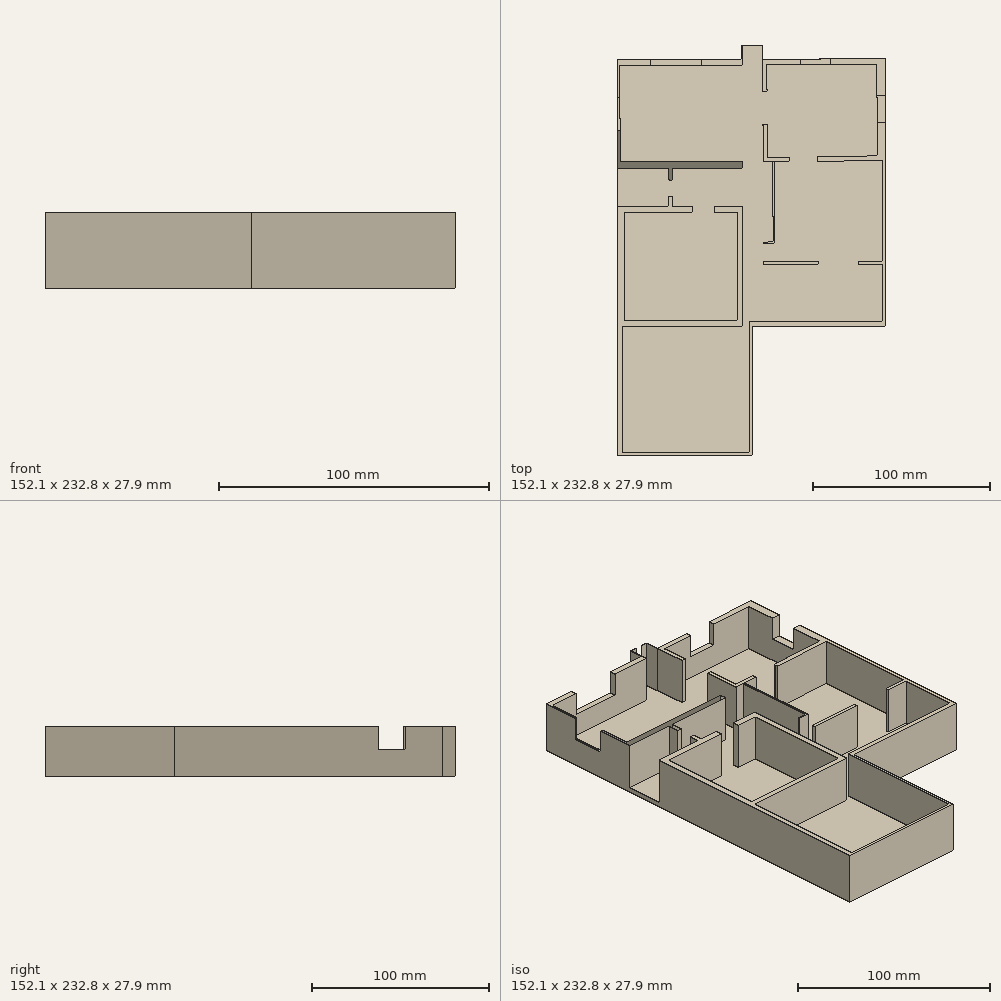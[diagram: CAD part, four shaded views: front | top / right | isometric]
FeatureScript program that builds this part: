
annotation { "Feature Type Name" : "Feature", "Feature Type Description" : "" }
export const myFeature = defineFeature(function(context is Context, id is Id, definition is map)
    precondition{}
    {
        {
            var Q0;
            Q0=qCreatedBy(makeId("Top.planeOp"),FACE);
            var sketch = newSketch(context, id + "F0", { "sketchPlane" : qUnion([Q0])});
            skLineSegment(sketch, "E0", {"start": v(0, 0) * mm, "end": v(0, 75.35) * mm});
            skLineSegment(sketch, "E1", {"start": v(0, 75.35) * mm, "end": v(-76.45, 75.35) * mm});
            skLineSegment(sketch, "E2", {"start": v(-76.45, 75.35) * mm, "end": v(-76.45, 0) * mm});
            skLineSegment(sketch, "E3", {"start": v(-76.45, 0) * mm, "end": v(-76.45, -76.07) * mm});
            skLineSegment(sketch, "E4", {"start": v(-76.45, -76.07) * mm, "end": v(0, -76.07) * mm});
            skLineSegment(sketch, "E5", {"start": v(0, -76.07) * mm, "end": v(0, 0) * mm});
            skLineSegment(sketch, "E6", {"start": v(0, -76.07) * mm, "end": v(75.68, -76.07) * mm});
            skLineSegment(sketch, "E7", {"start": v(75.68, -76.07) * mm, "end": v(75.68, 76.2) * mm});
            skLineSegment(sketch, "E8", {"start": v(75.68, 76.2) * mm, "end": v(0, 75.35) * mm});
            skLineSegment(sketch, "E9", {"start": v(0, 0) * mm, "end": v(75.68, 0) * mm});
            skLineSegment(sketch, "E10", {"start": v(0, 0) * mm, "end": v(-76.45, 0) * mm});
            skSolve(sketch);
        }
        {
            var Q0;
            Q0 = qSketchRegion(id + "F0", true);
            extrude(context, id + "F1", {"entities" : qUnion([Q0]), "depth" : 2.54 * mm, "offsetDistance" : 25.4 * mm});
        }
        {
            var Q0;
            Q0=makeQuery(id+"F1.opExtrude","CAP_FACE",FACE,{"disambiguationData":[OSD([sQuery(id+"F0.wireOp",EDGE,"E1"),sQuery(id+"F0.wireOp",EDGE,"E2"),sQuery(id+"F0.wireOp",EDGE,"E3"),sQuery(id+"F0.wireOp",EDGE,"E4"),sQuery(id+"F0.wireOp",EDGE,"E6"),sQuery(id+"F0.wireOp",EDGE,"E7"),sQuery(id+"F0.wireOp",EDGE,"E8")])],"isStart":false});
            var sketch = newSketch(context, id + "F2", { "sketchPlane" : qUnion([Q0])});
            skLineSegment(sketch, "E11.0", {"start": v(0, 0) * mm, "end": v(0, 75.35) * mm});
            skLineSegment(sketch, "E12.0", {"start": v(0, -76.07) * mm, "end": v(0, 0) * mm});
            skLineSegment(sketch, "E13", {"start": v(0, 75.35) * mm, "end": v(-5.93, 75.35) * mm});
            skLineSegment(sketch, "E14", {"start": v(-5.93, 75.35) * mm, "end": v(-5.93, 83.46) * mm});
            skLineSegment(sketch, "E15", {"start": v(-5.93, 83.46) * mm, "end": v(0, 83.46) * mm});
            skLineSegment(sketch, "E16", {"start": v(0, 83.46) * mm, "end": v(5.93, 83.46) * mm});
            skLineSegment(sketch, "E17", {"start": v(5.93, 83.46) * mm, "end": v(5.93, 75.35) * mm});
            skLineSegment(sketch, "E18", {"start": v(5.93, 75.35) * mm, "end": v(0, 75.35) * mm});
            skSolve(sketch);
        }
        {
            var Q0;
            Q0 = qSketchRegion(id + "F2", true);
            extrude(context, id + "F3", {"entities" : qUnion([Q0]), "operationType" : NewBodyOperationType.ADD, "oppositeDirection" : true, "depth" : 2.54 * mm, "offsetDistance" : 25.4 * mm});
        }
        {
            var Q0;
            Q0=makeQuery(id+"F3.boolean.opBoolean","MERGE",FACE,{"derivedFrom":[makeQuery(id+"F1.opExtrude","CAP_FACE",FACE,{"disambiguationData":[OSD([sQuery(id+"F0.wireOp",EDGE,"E1"),sQuery(id+"F0.wireOp",EDGE,"E2"),sQuery(id+"F0.wireOp",EDGE,"E3"),sQuery(id+"F0.wireOp",EDGE,"E4"),sQuery(id+"F0.wireOp",EDGE,"E6"),sQuery(id+"F0.wireOp",EDGE,"E7"),sQuery(id+"F0.wireOp",EDGE,"E8")])],"isStart":false}),makeQuery(id+"F3.opExtrude","CAP_FACE",FACE,{"disambiguationData":[OSD([sQuery(id+"F2.wireOp",EDGE,"E13"),sQuery(id+"F2.wireOp",EDGE,"E14"),sQuery(id+"F2.wireOp",EDGE,"E15"),sQuery(id+"F2.wireOp",EDGE,"E16"),sQuery(id+"F2.wireOp",EDGE,"E17"),sQuery(id+"F2.wireOp",EDGE,"E18")])],"isStart":true})]});
            var sketch = newSketch(context, id + "F4", { "sketchPlane" : qUnion([Q0])});
            skLineSegment(sketch, "E19.0", {"start": v(0, 0) * mm, "end": v(0, 75.35) * mm});
            skLineSegment(sketch, "E20.0", {"start": v(0, -76.07) * mm, "end": v(0, 0) * mm});
            skPoint(sketch, "E21.0", {"position": v(5.93, 75.42) * mm});
            skLineSegment(sketch, "E22", {"start": v(5.93, 75.42) * mm, "end": v(6.14, 57.18) * mm});
            skLineSegment(sketch, "E23", {"start": v(5.93, 75.42) * mm, "end": v(8.22, 75.45) * mm});
            skLineSegment(sketch, "E24", {"start": v(8.22, 75.45) * mm, "end": v(8.43, 57.18) * mm});
            skLineSegment(sketch, "E25", {"start": v(8.43, 57.18) * mm, "end": v(6.14, 57.18) * mm});
            skLineSegment(sketch, "E26", {"start": v(6.14, 38.62) * mm, "end": v(6.31, 22.93) * mm});
            skLineSegment(sketch, "E27", {"start": v(6.31, 22.93) * mm, "end": v(8.43, 22.96) * mm});
            skLineSegment(sketch, "E28", {"start": v(8.43, 22.96) * mm, "end": v(8.43, 38.62) * mm});
            skLineSegment(sketch, "E29", {"start": v(8.43, 38.62) * mm, "end": v(6.14, 38.62) * mm});
            skLineSegment(sketch, "E30", {"start": v(6.31, 22.93) * mm, "end": v(6.38, 17.54) * mm});
            skLineSegment(sketch, "E31", {"start": v(6.38, 17.54) * mm, "end": v(21.15, 17.71) * mm});
            skLineSegment(sketch, "E32", {"start": v(21.15, 17.71) * mm, "end": v(21.12, 19.99) * mm});
            skLineSegment(sketch, "E33", {"start": v(21.12, 19.99) * mm, "end": v(8.43, 19.84) * mm});
            skLineSegment(sketch, "E34", {"start": v(8.43, 19.84) * mm, "end": v(8.43, 22.96) * mm});
            skLineSegment(sketch, "E35", {"start": v(37.2, 17.71) * mm, "end": v(75.68, 18.15) * mm});
            skLineSegment(sketch, "E36", {"start": v(75.68, 18.15) * mm, "end": v(75.68, 19.99) * mm});
            skLineSegment(sketch, "E37", {"start": v(75.68, 19.99) * mm, "end": v(37.1, 19.55) * mm});
            skLineSegment(sketch, "E38", {"start": v(37.1, 19.55) * mm, "end": v(37.2, 17.71) * mm});
            skLineSegment(sketch, "E39", {"start": v(8.25, 72.63) * mm, "end": v(70.66, 72.63) * mm});
            skLineSegment(sketch, "E40", {"start": v(70.66, 72.63) * mm, "end": v(70.66, 76.15) * mm});
            skLineSegment(sketch, "E41", {"start": v(70.66, 76.15) * mm, "end": v(8.22, 75.45) * mm});
            skLineSegment(sketch, "E42", {"start": v(70.66, 72.63) * mm, "end": v(71.25, 19.99) * mm});
            skLineSegment(sketch, "E43", {"start": v(71.25, 19.99) * mm, "end": v(75.68, 19.99) * mm});
            skLineSegment(sketch, "E44", {"start": v(75.68, 19.99) * mm, "end": v(75.68, 76.2) * mm});
            skLineSegment(sketch, "E45", {"start": v(71.03, 39.78) * mm, "end": v(75.68, 39.83) * mm});
            skLineSegment(sketch, "E46", {"start": v(70.86, 55.15) * mm, "end": v(75.68, 55.15) * mm});
            skLineSegment(sketch, "E47", {"start": v(27.72, 72.63) * mm, "end": v(27.69, 75.67) * mm});
            skLineSegment(sketch, "E48", {"start": v(44.66, 72.63) * mm, "end": v(44.63, 75.86) * mm});
            skLineSegment(sketch, "E49", {"start": v(6.38, -38.96) * mm, "end": v(37.4, -38.96) * mm});
            skLineSegment(sketch, "E50", {"start": v(60.62, -38.96) * mm, "end": v(75.68, -38.96) * mm});
            skLineSegment(sketch, "E51", {"start": v(75.68, -38.96) * mm, "end": v(75.68, 18.15) * mm});
            skLineSegment(sketch, "E52", {"start": v(6.38, -38.96) * mm, "end": v(6.38, -46.95) * mm});
            skLineSegment(sketch, "E53", {"start": v(6.38, -76.07) * mm, "end": v(75.68, -76.07) * mm});
            skLineSegment(sketch, "E54", {"start": v(75.68, -76.07) * mm, "end": v(75.68, -38.96) * mm});
            skLineSegment(sketch, "E55", {"start": v(8.43, -28.89) * mm, "end": v(6.38, -28.89) * mm});
            skLineSegment(sketch, "E56", {"start": v(73.78, 18.13) * mm, "end": v(73.78, -38.96) * mm});
            skLineSegment(sketch, "E57", {"start": v(6.38, -40.7) * mm, "end": v(37.4, -40.7) * mm});
            skLineSegment(sketch, "E58", {"start": v(37.4, -40.7) * mm, "end": v(37.4, -38.96) * mm});
            skLineSegment(sketch, "E59", {"start": v(60.62, -40.7) * mm, "end": v(75.68, -40.7) * mm});
            skLineSegment(sketch, "E60", {"start": v(60.62, -40.7) * mm, "end": v(60.62, -38.96) * mm});
            skLineSegment(sketch, "E61", {"start": v(73.78, -40.7) * mm, "end": v(73.78, -73.26) * mm});
            skLineSegment(sketch, "E62", {"start": v(73.78, -73.26) * mm, "end": v(6.38, -73.26) * mm});
            skLineSegment(sketch, "E63", {"start": v(6.38, -73.26) * mm, "end": v(6.38, -76.07) * mm});
            skLineSegment(sketch, "E64", {"start": v(-5.93, 83.46) * mm, "end": v(-2.26, 83.46) * mm});
            skLineSegment(sketch, "E65", {"start": v(-5.46, 82.76) * mm, "end": v(-5.93, 82.76) * mm});
            skLineSegment(sketch, "E66", {"start": v(-5.93, 82.76) * mm, "end": v(-5.93, 83.46) * mm});
            skLineSegment(sketch, "E67", {"start": v(-5.93, 82.76) * mm, "end": v(-5.93, 75.35) * mm});
            skLineSegment(sketch, "E68", {"start": v(-5.93, 75.35) * mm, "end": v(-5.46, 75.35) * mm});
            skLineSegment(sketch, "E69", {"start": v(-5.46, 75.35) * mm, "end": v(-5.46, 82.76) * mm});
            skLineSegment(sketch, "E70", {"start": v(5.93, 75.42) * mm, "end": v(5.93, 83.46) * mm});
            skLineSegment(sketch, "E71", {"start": v(5.93, 83.46) * mm, "end": v(1.63, 83.46) * mm});
            skLineSegment(sketch, "E72", {"start": v(-5.93, 75.35) * mm, "end": v(-76.45, 75.35) * mm});
            skLineSegment(sketch, "E73", {"start": v(-76.45, 75.35) * mm, "end": v(-76.45, 71.98) * mm});
            skLineSegment(sketch, "E74", {"start": v(-76.45, 71.98) * mm, "end": v(-5.46, 71.98) * mm});
            skLineSegment(sketch, "E75", {"start": v(-5.46, 71.98) * mm, "end": v(-5.46, 75.35) * mm});
            skLineSegment(sketch, "E76", {"start": v(-5.46, 17.54) * mm, "end": v(-76.45, 17.54) * mm});
            skLineSegment(sketch, "E77", {"start": v(-5.46, 17.54) * mm, "end": v(-5.41, 13.55) * mm});
            skLineSegment(sketch, "E78", {"start": v(-5.41, 13.55) * mm, "end": v(-76.45, 13.55) * mm});
            skLineSegment(sketch, "E79", {"start": v(-76.45, 13.55) * mm, "end": v(-76.45, 17.54) * mm});
            skLineSegment(sketch, "E80", {"start": v(-5.41, -7.79) * mm, "end": v(-21.24, -7.97) * mm});
            skLineSegment(sketch, "E81", {"start": v(-5.41, -7.79) * mm, "end": v(-5.41, -76.07) * mm});
            skLineSegment(sketch, "E82", {"start": v(-33.79, -7.97) * mm, "end": v(-76.45, -7.97) * mm});
            skLineSegment(sketch, "E83", {"start": v(-76.45, -7.97) * mm, "end": v(-76.45, -11.38) * mm});
            skLineSegment(sketch, "E84", {"start": v(-76.45, -11.38) * mm, "end": v(-33.79, -11.38) * mm});
            skLineSegment(sketch, "E85", {"start": v(-33.79, -11.38) * mm, "end": v(-33.79, -7.97) * mm});
            skLineSegment(sketch, "E86", {"start": v(-21.24, -11.38) * mm, "end": v(-8.58, -11.38) * mm});
            skLineSegment(sketch, "E87", {"start": v(-8.58, -11.38) * mm, "end": v(-8.58, -76.07) * mm});
            skLineSegment(sketch, "E88", {"start": v(-8.58, -76.07) * mm, "end": v(-5.41, -76.07) * mm});
            skLineSegment(sketch, "E89", {"start": v(-21.24, -11.38) * mm, "end": v(-21.24, -7.97) * mm});
            skLineSegment(sketch, "E90", {"start": v(-72.71, -11.38) * mm, "end": v(-72.71, -72.9) * mm});
            skLineSegment(sketch, "E91", {"start": v(-72.71, -72.9) * mm, "end": v(-8.58, -72.9) * mm});
            skLineSegment(sketch, "E92.0", {"start": v(75.68, 76.2) * mm, "end": v(0, 75.35) * mm});
            skLineSegment(sketch, "E93.0", {"start": v(-76.45, 0) * mm, "end": v(-76.45, -76.07) * mm});
            skLineSegment(sketch, "E94", {"start": v(-44.97, 13.55) * mm, "end": v(-44.97, 7) * mm});
            skLineSegment(sketch, "E95", {"start": v(-44.97, -7.97) * mm, "end": v(-44.97, -2.33) * mm});
            skLineSegment(sketch, "E96", {"start": v(-47.46, 13.55) * mm, "end": v(-47.46, 7.13) * mm});
            skLineSegment(sketch, "E97", {"start": v(-44.97, 7) * mm, "end": v(-47.46, 7.13) * mm});
            skLineSegment(sketch, "E98", {"start": v(-44.97, -2.33) * mm, "end": v(-47.46, -2.33) * mm});
            skLineSegment(sketch, "E99", {"start": v(-47.46, -2.33) * mm, "end": v(-47.46, -7.97) * mm});
            skLineSegment(sketch, "E100", {"start": v(75.68, 19.99) * mm, "end": v(75.68, 39.83) * mm});
            skLineSegment(sketch, "E101", {"start": v(75.68, 39.83) * mm, "end": v(75.68, 55.15) * mm});
            skLineSegment(sketch, "E102", {"start": v(75.68, 55.15) * mm, "end": v(75.68, 76.2) * mm});
            skLineSegment(sketch, "E103", {"start": v(8.22, 75.45) * mm, "end": v(27.69, 75.67) * mm});
            skLineSegment(sketch, "E104", {"start": v(27.69, 75.67) * mm, "end": v(44.63, 75.86) * mm});
            skLineSegment(sketch, "E105", {"start": v(44.63, 75.86) * mm, "end": v(70.66, 76.15) * mm});
            skLineSegment(sketch, "E106", {"start": v(70.66, 76.15) * mm, "end": v(75.68, 76.2) * mm});
            skLineSegment(sketch, "E107", {"start": v(75.79, 76.24) * mm, "end": v(75.68, 55.15) * mm});
            skLineSegment(sketch, "E108", {"start": v(-75.4, 71.98) * mm, "end": v(-74.78, 17.54) * mm});
            skLineSegment(sketch, "E109", {"start": v(-76.45, 17.54) * mm, "end": v(-76.45, 71.98) * mm});
            skLineSegment(sketch, "E110", {"start": v(-75.2, 54.08) * mm, "end": v(-76.45, 54.08) * mm});
            skLineSegment(sketch, "E111", {"start": v(-76.45, 54.08) * mm, "end": v(-76.45, 35.02) * mm});
            skLineSegment(sketch, "E112", {"start": v(-76.45, 35.02) * mm, "end": v(-74.98, 35.04) * mm});
            skLineSegment(sketch, "E113", {"start": v(-74.98, 35.04) * mm, "end": v(-75.2, 54.08) * mm});
            skLineSegment(sketch, "E114", {"start": v(-72.71, -23.63) * mm, "end": v(-76.45, -23.63) * mm});
            skLineSegment(sketch, "E115", {"start": v(-76.45, -23.63) * mm, "end": v(-76.45, -32.25) * mm});
            skLineSegment(sketch, "E116", {"start": v(-76.45, -32.25) * mm, "end": v(-72.71, -32.2) * mm});
            skLineSegment(sketch, "E117", {"start": v(-72.71, -32.2) * mm, "end": v(-72.71, -23.63) * mm});
            skLineSegment(sketch, "E118", {"start": v(20.11, -73.26) * mm, "end": v(20.14, -76.07) * mm});
            skLineSegment(sketch, "E119", {"start": v(20.14, -76.07) * mm, "end": v(56.16, -76.07) * mm});
            skLineSegment(sketch, "E120", {"start": v(56.16, -76.07) * mm, "end": v(56.13, -73.26) * mm});
            skLineSegment(sketch, "E121", {"start": v(56.13, -73.26) * mm, "end": v(20.11, -73.26) * mm});
            skLineSegment(sketch, "E122", {"start": v(-28.91, 75.35) * mm, "end": v(-28.91, 71.98) * mm});
            skLineSegment(sketch, "E123", {"start": v(-28.91, 71.98) * mm, "end": v(-57.74, 71.98) * mm});
            skLineSegment(sketch, "E124", {"start": v(-57.74, 71.98) * mm, "end": v(-57.74, 75.35) * mm});
            skLineSegment(sketch, "E125", {"start": v(-76.45, 0) * mm, "end": v(-76.45, 13.55) * mm});
            skLineSegment(sketch, "E126", {"start": v(-76.45, 13.55) * mm, "end": v(-76.45, -7.97) * mm});
            skLineSegment(sketch, "E127", {"start": v(-76.45, -7.97) * mm, "end": v(-75.89, -7.97) * mm});
            skLineSegment(sketch, "E128", {"start": v(-75.89, -7.97) * mm, "end": v(-75.89, 13.55) * mm});
            skLineSegment(sketch, "E129", {"start": v(-75.89, 13.55) * mm, "end": v(-76.45, 13.55) * mm});
            skLineSegment(sketch, "E130", {"start": v(6.38, -73.26) * mm, "end": v(0, -73.26) * mm});
            skLineSegment(sketch, "E131", {"start": v(0, -73.26) * mm, "end": v(0, -76.07) * mm});
            skLineSegment(sketch, "E132", {"start": v(0, -76.07) * mm, "end": v(6.38, -76.07) * mm});
            skPoint(sketch, "E133.end.orphan", {"position": v(1.63, 82.76) * mm});
            skLineSegment(sketch, "E134", {"start": v(-5.46, 82.76) * mm, "end": v(-5.46, 83.2) * mm});
            skLineSegment(sketch, "E135", {"start": v(-5.46, 83.2) * mm, "end": v(-2.26, 83.2) * mm});
            skLineSegment(sketch, "E136", {"start": v(-2.26, 83.2) * mm, "end": v(-2.26, 83.46) * mm});
            skLineSegment(sketch, "E137", {"start": v(1.63, 83.2) * mm, "end": v(5.69, 83.2) * mm});
            skLineSegment(sketch, "E138", {"start": v(5.69, 83.2) * mm, "end": v(5.69, 75.42) * mm});
            skLineSegment(sketch, "E139", {"start": v(1.63, 83.46) * mm, "end": v(1.63, 83.2) * mm});
            skPoint(sketch, "E140.end.orphan", {"position": v(5.34, 75.35) * mm});
            skLineSegment(sketch, "E141", {"start": v(5.69, 75.42) * mm, "end": v(5.93, 75.42) * mm});
            skPoint(sketch, "E142.start.orphan", {"position": v(8.43, 17.57) * mm});
            skLineSegment(sketch, "E143", {"start": v(8.43, -28.89) * mm, "end": v(12.92, -28.89) * mm});
            skLineSegment(sketch, "E144", {"start": v(12.92, -28.89) * mm, "end": v(12.4, 17.61) * mm});
            skLineSegment(sketch, "E145", {"start": v(12.4, 17.61) * mm, "end": v(11.47, 17.6) * mm});
            skLineSegment(sketch, "E146", {"start": v(11.47, 17.6) * mm, "end": v(12, -28.89) * mm});
            skLineSegment(sketch, "E147", {"start": v(12, -28.89) * mm, "end": v(12.92, -28.89) * mm});
            skSolve(sketch);
        }
        {
            var Q0;
            Q0=makeQuery(id+"F0.imprint","IMPRINT",FACE,{"disambiguationData":[TD([[makeQuery(id+"F0.imprint","IMPRINT",EDGE,{"derivedFrom":sQuery(id+"F0.wireOp",EDGE,"E0")}),-1.0]])]});
            var sketch = newSketch(context, id + "F5", { "sketchPlane" : qUnion([Q0])});
            skLineSegment(sketch, "E148.0", {"start": v(0, -76.07) * mm, "end": v(75.68, -76.07) * mm});
            skLineSegment(sketch, "E149.0.3", {"start": v(-72.71, -11.38) * mm, "end": v(-76.45, -11.38) * mm});
            skLineSegment(sketch, "E149.0.4", {"start": v(-76.45, -11.38) * mm, "end": v(-76.45, -23.63) * mm});
            skLineSegment(sketch, "E150", {"start": v(0, -76.07) * mm, "end": v(0, -149.33) * mm});
            skLineSegment(sketch, "E151", {"start": v(0, -149.33) * mm, "end": v(-76.45, -149.33) * mm});
            skLineSegment(sketch, "E152", {"start": v(-76.45, -149.33) * mm, "end": v(-76.45, -23.63) * mm});
            skLineSegment(sketch, "E153", {"start": v(0, -76.07) * mm, "end": v(-76.45, -76.07) * mm});
            skPoint(sketch, "E149.0.0.start.orphan", {"position": v(-8.58, -23.63) * mm});
            skSolve(sketch);
        }
        {
            var Q0;
            {var subQ3=sQuery(id+"F5.wireOp",EDGE,"E150");Q0=makeQuery(id+"F5.imprint","IMPRINT",FACE,{"disambiguationData":[TD([[makeQuery(id+"F5.imprint","IMPRINT",EDGE,{"derivedFrom":subQ3}),-1.0]])]});}
            extrude(context, id + "F6", {"entities" : qUnion([Q0]), "operationType" : NewBodyOperationType.ADD, "depth" : 2.54 * mm, "offsetDistance" : 25.4 * mm});
        }
        {
            var Q0;
            Q0=makeQuery(id+"F6.boolean.opBoolean","MERGE",FACE,{"derivedFrom":[makeQuery(id+"F3.boolean.opBoolean","MERGE",FACE,{"derivedFrom":[makeQuery(id+"F1.opExtrude","CAP_FACE",FACE,{"disambiguationData":[OSD([sQuery(id+"F0.wireOp",EDGE,"E1"),sQuery(id+"F0.wireOp",EDGE,"E2"),sQuery(id+"F0.wireOp",EDGE,"E3"),sQuery(id+"F0.wireOp",EDGE,"E4"),sQuery(id+"F0.wireOp",EDGE,"E6"),sQuery(id+"F0.wireOp",EDGE,"E7"),sQuery(id+"F0.wireOp",EDGE,"E8")])],"isStart":false}),makeQuery(id+"F3.opExtrude","CAP_FACE",FACE,{"disambiguationData":[OSD([sQuery(id+"F2.wireOp",EDGE,"E13"),sQuery(id+"F2.wireOp",EDGE,"E14"),sQuery(id+"F2.wireOp",EDGE,"E15"),sQuery(id+"F2.wireOp",EDGE,"E16"),sQuery(id+"F2.wireOp",EDGE,"E17"),sQuery(id+"F2.wireOp",EDGE,"E18")])],"isStart":true})]}),makeQuery(id+"F6.opExtrude","CAP_FACE",FACE,{"disambiguationData":[OSD([sQuery(id+"F5.wireOp",EDGE,"E150"),sQuery(id+"F5.wireOp",EDGE,"E151"),sQuery(id+"F5.wireOp",EDGE,"E152"),sQuery(id+"F5.wireOp",EDGE,"dPd2rH2K-U4fC-YkTU-IFvo-9luxmJDQ5Bo5")])],"isStart":false})]});
            var sketch = newSketch(context, id + "F7", { "sketchPlane" : qUnion([Q0])});
            skPoint(sketch, "E154.0", {"position": v(-8.58, -76.07) * mm});
            skLineSegment(sketch, "E155.0", {"start": v(-5.41, -7.79) * mm, "end": v(-5.41, -76.07) * mm});
            skPoint(sketch, "E156.0", {"position": v(0, -76.07) * mm});
            skLineSegment(sketch, "E157", {"start": v(-8.58, -76.07) * mm, "end": v(-76.45, -76.07) * mm});
            skLineSegment(sketch, "E158", {"start": v(-73.46, -76.07) * mm, "end": v(-73.46, -147.77) * mm});
            skLineSegment(sketch, "E159", {"start": v(-73.46, -147.77) * mm, "end": v(-1.4, -147.77) * mm});
            skLineSegment(sketch, "E160", {"start": v(-1.4, -147.77) * mm, "end": v(-1.4, -76.07) * mm});
            skLineSegment(sketch, "E161", {"start": v(-1.4, -76.07) * mm, "end": v(0, -76.07) * mm});
            skLineSegment(sketch, "E162", {"start": v(-5.41, -76.07) * mm, "end": v(-8.58, -76.07) * mm});
            skLineSegment(sketch, "E163.0", {"start": v(0, -76.07) * mm, "end": v(0, 0) * mm});
            skPoint(sketch, "E164.0", {"position": v(0, -73.26) * mm});
            skLineSegment(sketch, "E165", {"start": v(0, -73.26) * mm, "end": v(-1.4, -73.26) * mm});
            skLineSegment(sketch, "E166", {"start": v(-1.4, -73.26) * mm, "end": v(-1.4, -76.07) * mm});
            skSolve(sketch);
        }
        {
            var Q0;
            {var subQ0=sQuery(id+"F7.wireOp",EDGE,"E158");Q0=makeQuery(id+"F7.imprint","IMPRINT",FACE,{"disambiguationData":[TD([[makeQuery(id+"F7.imprint","IMPRINT",EDGE,{"derivedFrom":subQ0}),-1.0]])]});}
            var Q1;
            {var subQ1=sQuery(id+"F4.wireOp",EDGE,"E90");Q1=makeQuery(id+"F4.imprint","IMPRINT",FACE,{"disambiguationData":[TD([[makeQuery(id+"F4.imprint","IMPRINT",EDGE,{"derivedFrom":subQ1}),-1.0]])]});}
            var Q2;
            {var subQ4=sQuery(id+"F4.wireOp",EDGE,"E53");Q2=makeQuery(id+"F4.imprint","IMPRINT",FACE,{"disambiguationData":[TD([[makeQuery(id+"F4.imprint","IMPRINT",EDGE,{"derivedFrom":subQ4}),1.0]])]});}
            var Q3;
            {var subQ0=sQuery(id+"F4.wireOp",EDGE,"E60");Q3=makeQuery(id+"F4.imprint","IMPRINT",FACE,{"disambiguationData":[TD([[makeQuery(id+"F4.imprint","IMPRINT",EDGE,{"derivedFrom":subQ0}),-1.0]])]});}
            var Q4;
            {var subQ0=sQuery(id+"F4.wireOp",EDGE,"E49");Q4=makeQuery(id+"F4.imprint","IMPRINT",FACE,{"disambiguationData":[TD([[makeQuery(id+"F4.imprint","IMPRINT",EDGE,{"derivedFrom":subQ0}),-1.0]])]});}
            var Q5;
            {var subQ0=sQuery(id+"F4.wireOp",EDGE,"E51");Q5=makeQuery(id+"F4.imprint","IMPRINT",FACE,{"disambiguationData":[TD([[makeQuery(id+"F4.imprint","IMPRINT",EDGE,{"derivedFrom":subQ0}),1.0]])]});}
            var Q6;
            Q6=makeQuery(id+"F4.imprint","IMPRINT",FACE,{"disambiguationData":[TD([[makeQuery(id+"F4.imprint","IMPRINT",EDGE,{"derivedFrom":sQuery(id+"F4.wireOp",EDGE,"E80")}),1.0]])]});
            var Q7;
            {var subQ8=sQuery(id+"F4.wireOp",EDGE,"E85");Q7=makeQuery(id+"F4.imprint","IMPRINT",FACE,{"disambiguationData":[TD([[makeQuery(id+"F4.imprint","IMPRINT",EDGE,{"derivedFrom":subQ8}),1.0]])]});}
            var Q8;
            {var subQ0=sQuery(id+"F4.wireOp",EDGE,"E95");Q8=makeQuery(id+"F4.imprint","IMPRINT",FACE,{"disambiguationData":[TD([[makeQuery(id+"F4.imprint","IMPRINT",EDGE,{"derivedFrom":subQ0}),1.0]])]});}
            var Q9;
            {var subQ0=sQuery(id+"F4.wireOp",EDGE,"E94");Q9=makeQuery(id+"F4.imprint","IMPRINT",FACE,{"disambiguationData":[TD([[makeQuery(id+"F4.imprint","IMPRINT",EDGE,{"derivedFrom":subQ0}),-1.0]])]});}
            var Q10;
            Q10=makeQuery(id+"F4.imprint","IMPRINT",FACE,{"disambiguationData":[TD([[makeQuery(id+"F4.imprint","IMPRINT",EDGE,{"derivedFrom":sQuery(id+"F4.wireOp",EDGE,"E76")}),1.0]])]});
            var Q11;
            {var subQ0=sQuery(id+"F4.wireOp",EDGE,"LhCe9oIa-q0IU-38Dy-E6zw-4cbbR9uXmgjQ");Q11=makeQuery(id+"F4.imprint","IMPRINT",FACE,{"disambiguationData":[TD([[makeQuery(id+"F4.imprint","IMPRINT",EDGE,{"derivedFrom":subQ0}),1.0]])]});}
            var Q12;
            Q12=makeQuery(id+"F4.imprint","IMPRINT",FACE,{"disambiguationData":[TD([[makeQuery(id+"F4.imprint","IMPRINT",EDGE,{"derivedFrom":sQuery(id+"F4.wireOp",EDGE,"E27")}),-1.0]])]});
            var Q13;
            Q13=makeQuery(id+"F4.imprint","IMPRINT",FACE,{"disambiguationData":[TD([[makeQuery(id+"F4.imprint","IMPRINT",EDGE,{"derivedFrom":sQuery(id+"F4.wireOp",EDGE,"E26")}),1.0]])]});
            var Q14;
            {var subQ0=sQuery(id+"F4.wireOp",EDGE,"E36");Q14=makeQuery(id+"F4.imprint","IMPRINT",FACE,{"disambiguationData":[TD([[makeQuery(id+"F4.imprint","IMPRINT",EDGE,{"derivedFrom":subQ0}),1.0]])]});}
            var Q15;
            {var subQ5=sQuery(id+"F4.wireOp",EDGE,"E22");Q15=makeQuery(id+"F4.imprint","IMPRINT",FACE,{"disambiguationData":[TD([[makeQuery(id+"F4.imprint","IMPRINT",EDGE,{"derivedFrom":subQ5}),1.0]])]});}
            var Q16;
            {var subQ4=sQuery(id+"F4.wireOp",EDGE,"E91");Q16=makeQuery(id+"F4.imprint","IMPRINT",FACE,{"disambiguationData":[TD([[makeQuery(id+"F4.imprint","IMPRINT",EDGE,{"derivedFrom":subQ4}),-1.0]])]});}
            var Q17;
            {var subQ3=sQuery(id+"F4.wireOp",EDGE,"E61");Q17=makeQuery(id+"F4.imprint","IMPRINT",FACE,{"disambiguationData":[TD([[makeQuery(id+"F4.imprint","IMPRINT",EDGE,{"derivedFrom":subQ3}),1.0]])]});}
            var Q18;
            {var subQ4=sQuery(id+"F4.wireOp",EDGE,"E68");Q18=makeQuery(id+"F4.imprint","IMPRINT",FACE,{"disambiguationData":[TD([[makeQuery(id+"F4.imprint","IMPRINT",EDGE,{"derivedFrom":subQ4}),-1.0]])]});}
            var Q19;
            Q19=makeQuery(id+"F4.imprint","IMPRINT",FACE,{"disambiguationData":[TD([[makeQuery(id+"F4.imprint","IMPRINT",EDGE,{"derivedFrom":sQuery(id+"F4.wireOp",EDGE,"E67")}),-1.0]])]});
            var Q20;
            Q20=makeQuery(id+"F4.imprint","IMPRINT",FACE,{"disambiguationData":[TD([[makeQuery(id+"F4.imprint","IMPRINT",EDGE,{"derivedFrom":sQuery(id+"F4.wireOp",EDGE,"E64")}),-1.0]])]});
            var Q21;
            {var subQ3=sQuery(id+"F4.wireOp",EDGE,"E73");Q21=makeQuery(id+"F4.imprint","IMPRINT",FACE,{"disambiguationData":[TD([[makeQuery(id+"F4.imprint","IMPRINT",EDGE,{"derivedFrom":subQ3}),1.0]])]});}
            var Q22;
            {var subQ5=sQuery(id+"F4.wireOp",EDGE,"E110");Q22=makeQuery(id+"F4.imprint","IMPRINT",FACE,{"disambiguationData":[TD([[makeQuery(id+"F4.imprint","IMPRINT",EDGE,{"derivedFrom":subQ5}),-1.0]])]});}
            var Q23;
            {var subQ5=sQuery(id+"F4.wireOp",EDGE,"E112");Q23=makeQuery(id+"F4.imprint","IMPRINT",FACE,{"disambiguationData":[TD([[makeQuery(id+"F4.imprint","IMPRINT",EDGE,{"derivedFrom":subQ5}),-1.0]])]});}
            var Q24;
            Q24=makeQuery(id+"F4.imprint","IMPRINT",FACE,{"disambiguationData":[TD([[makeQuery(id+"F4.imprint","IMPRINT",EDGE,{"derivedFrom":sQuery(id+"F4.wireOp",EDGE,"E126")}),1.0]])]});
            var Q25;
            Q25=makeQuery(id+"F4.imprint","IMPRINT",FACE,{"disambiguationData":[TD([[makeQuery(id+"F4.imprint","IMPRINT",EDGE,{"derivedFrom":sQuery(id+"F4.wireOp",EDGE,"E63")}),-1.0]])]});
            var Q26;
            {var subQ0=sQuery(id+"F7.wireOp",EDGE,"E161");Q26=makeQuery(id+"F7.imprint","IMPRINT",FACE,{"disambiguationData":[TD([[makeQuery(id+"F7.imprint","IMPRINT",EDGE,{"derivedFrom":subQ0}),1.0]])]});}
            extrude(context, id + "F8", {"entities" : qUnion([Q0, Q1, Q2, Q3, Q4, Q5, Q6, Q7, Q8, Q9, Q10, Q11, Q12, Q13, Q14, Q15, Q16, Q17, Q18, Q19, Q20, Q21, Q22, Q23, Q24, Q25, Q26]), "operationType" : NewBodyOperationType.ADD, "depth" : 25.4 * mm, "offsetDistance" : 25.4 * mm});
        }
        {
            var Q0;
            {var subQ0=sQuery(id+"F4.wireOp",EDGE,"E45");Q0=makeQuery(id+"F4.imprint","IMPRINT",FACE,{"disambiguationData":[TD([[makeQuery(id+"F4.imprint","IMPRINT",EDGE,{"derivedFrom":subQ0}),1.0]])]});}
            var Q1;
            {var subQ0=sQuery(id+"F4.wireOp",EDGE,"E47");Q1=makeQuery(id+"F4.imprint","IMPRINT",FACE,{"disambiguationData":[TD([[makeQuery(id+"F4.imprint","IMPRINT",EDGE,{"derivedFrom":subQ0}),-1.0]])]});}
            var Q2;
            Q2=makeQuery(id+"F4.imprint","IMPRINT",FACE,{"disambiguationData":[TD([[makeQuery(id+"F4.imprint","IMPRINT",EDGE,{"derivedFrom":sQuery(id+"F4.wireOp",EDGE,"E110")}),1.0]])]});
            var Q3;
            {var subQ0=sQuery(id+"F4.wireOp",EDGE,"E122");Q3=makeQuery(id+"F4.imprint","IMPRINT",FACE,{"disambiguationData":[TD([[makeQuery(id+"F4.imprint","IMPRINT",EDGE,{"derivedFrom":subQ0}),-1.0]])]});}
            var Q4;
            Q4=makeQuery(id+"F4.imprint","IMPRINT",FACE,{"disambiguationData":[TD([[makeQuery(id+"F4.imprint","IMPRINT",EDGE,{"derivedFrom":sQuery(id+"F4.wireOp",EDGE,"E114")}),1.0]])]});
            var Q5;
            Q5=makeQuery(id+"F4.imprint","IMPRINT",FACE,{"disambiguationData":[TD([[makeQuery(id+"F4.imprint","IMPRINT",EDGE,{"derivedFrom":sQuery(id+"F4.wireOp",EDGE,"E118")}),1.0]])]});
            extrude(context, id + "F9", {"entities" : qUnion([Q0, Q1, Q2, Q3, Q4, Q5]), "operationType" : NewBodyOperationType.ADD, "depth" : 12.7 * mm, "offsetDistance" : 25.4 * mm});
        }
        {
            var Q0;
            {var subQ22=sQuery(id+"F4.wireOp",EDGE,"E19.0");Q0=makeQuery(id+"F4.imprint","IMPRINT",FACE,{"disambiguationData":[TD([[makeQuery(id+"F4.imprint","IMPRINT",EDGE,{"derivedFrom":subQ22}),-1.0]])]});}
            var sketch = newSketch(context, id + "F10", { "sketchPlane" : qUnion([Q0])});
            skLineSegment(sketch, "E167.0", {"start": v(70.66, 72.63) * mm, "end": v(71.25, 19.99) * mm});
            skLineSegment(sketch, "E168.0", {"start": v(75.68, 19.99) * mm, "end": v(75.68, 39.83) * mm});
            skLineSegment(sketch, "E169.0", {"start": v(71.25, 19.99) * mm, "end": v(75.68, 19.99) * mm});
            skLineSegment(sketch, "E170.0", {"start": v(71.03, 39.78) * mm, "end": v(75.68, 39.83) * mm});
            skLineSegment(sketch, "E171.0", {"start": v(70.86, 55.15) * mm, "end": v(75.68, 55.15) * mm});
            skLineSegment(sketch, "E172.0", {"start": v(75.79, 76.24) * mm, "end": v(75.68, 55.15) * mm});
            skLineSegment(sketch, "E173.0", {"start": v(70.66, 76.15) * mm, "end": v(75.68, 76.2) * mm});
            skLineSegment(sketch, "E174.0", {"start": v(8.25, 72.63) * mm, "end": v(70.66, 72.63) * mm});
            skPoint(sketch, "E175.0", {"position": v(70.66, 74.39) * mm});
            skLineSegment(sketch, "E176.0", {"start": v(70.66, 72.63) * mm, "end": v(70.66, 76.15) * mm});
            skLineSegment(sketch, "E177.0", {"start": v(70.66, 76.15) * mm, "end": v(8.22, 75.45) * mm});
            skLineSegment(sketch, "E178.0", {"start": v(44.66, 72.63) * mm, "end": v(44.63, 75.86) * mm});
            skLineSegment(sketch, "E179.0", {"start": v(8.22, 75.45) * mm, "end": v(8.43, 57.18) * mm});
            skLineSegment(sketch, "E180.0", {"start": v(27.72, 72.63) * mm, "end": v(27.69, 75.67) * mm});
            skLineSegment(sketch, "E181.0", {"start": v(75.68, 19.99) * mm, "end": v(37.1, 19.55) * mm});
            skLineSegment(sketch, "E182", {"start": v(71.24, 20.79) * mm, "end": v(37.1, 20.4) * mm});
            skLineSegment(sketch, "E183", {"start": v(37.1, 20.4) * mm, "end": v(37.1, 19.55) * mm});
            skSolve(sketch);
        }
        {
            var Q0;
            {var subQ4=sQuery(id+"F4.wireOp",EDGE,"E47");Q0=makeQuery(id+"F4.imprint","IMPRINT",FACE,{"disambiguationData":[TD([[makeQuery(id+"F4.imprint","IMPRINT",EDGE,{"derivedFrom":subQ4}),1.0]])]});}
            var Q1;
            {var subQ0=sQuery(id+"F4.wireOp",EDGE,"E40");Q1=makeQuery(id+"F4.imprint","IMPRINT",FACE,{"disambiguationData":[TD([[makeQuery(id+"F4.imprint","IMPRINT",EDGE,{"derivedFrom":subQ0}),1.0]])]});}
            var Q2;
            {var subQ1=sQuery(id+"F4.wireOp",EDGE,"E40");Q2=makeQuery(id+"F4.imprint","IMPRINT",FACE,{"disambiguationData":[TD([[makeQuery(id+"F4.imprint","IMPRINT",EDGE,{"derivedFrom":subQ1}),-1.0]])]});}
            var Q3;
            {var subQ0=sQuery(id+"F4.wireOp",EDGE,"E43");Q3=makeQuery(id+"F4.imprint","IMPRINT",FACE,{"disambiguationData":[TD([[makeQuery(id+"F4.imprint","IMPRINT",EDGE,{"derivedFrom":subQ0}),1.0]])]});}
            var Q4;
            {var subQ1=sQuery(id+"F10.wireOp",EDGE,"E169.0");Q4=makeQuery(id+"F10.imprint","IMPRINT",FACE,{"disambiguationData":[TD([[makeQuery(id+"F10.imprint","IMPRINT",EDGE,{"derivedFrom":subQ1}),-1.0]])]});}
            extrude(context, id + "F11", {"entities" : qUnion([Q0, Q1, Q2, Q3, Q4]), "operationType" : NewBodyOperationType.ADD, "depth" : 25.4 * mm, "offsetDistance" : 25.4 * mm});
        }
        {
            var Q0;
            Q0=makeQuery(id+"F4.imprint","IMPRINT",FACE,{"disambiguationData":[TD([[makeQuery(id+"F4.imprint","IMPRINT",EDGE,{"derivedFrom":sQuery(id+"F4.wireOp",EDGE,"E137")}),1.0]])]});
            var sketch = newSketch(context, id + "F12", { "sketchPlane" : qUnion([Q0])});
            skLineSegment(sketch, "E184.0", {"start": v(5.69, 83.2) * mm, "end": v(5.69, 75.42) * mm});
            skLineSegment(sketch, "E185.0", {"start": v(5.93, 75.42) * mm, "end": v(5.93, 83.46) * mm});
            skLineSegment(sketch, "E186.0", {"start": v(5.93, 83.46) * mm, "end": v(1.63, 83.46) * mm});
            skLineSegment(sketch, "E187.0", {"start": v(1.63, 83.2) * mm, "end": v(5.69, 83.2) * mm});
            skLineSegment(sketch, "E188.0", {"start": v(1.63, 83.46) * mm, "end": v(1.63, 83.2) * mm});
            skLineSegment(sketch, "E189.0", {"start": v(75.68, 76.2) * mm, "end": v(0, 75.35) * mm});
            skLineSegment(sketch, "E190", {"start": v(5.93, 75.42) * mm, "end": v(6.14, 57.18) * mm});
            skLineSegment(sketch, "E191", {"start": v(6.14, 57.18) * mm, "end": v(6.1, 57.18) * mm});
            skLineSegment(sketch, "E192", {"start": v(6.1, 57.18) * mm, "end": v(5.9, 75.42) * mm});
            skLineSegment(sketch, "E193", {"start": v(5.9, 75.42) * mm, "end": v(5.93, 75.42) * mm});
            skSolve(sketch);
        }
        {
            var Q0;
            Q0 = qSketchRegion(id + "F12", true);
            extrude(context, id + "F13", {"entities" : qUnion([Q0]), "operationType" : NewBodyOperationType.ADD, "depth" : 25.4 * mm, "offsetDistance" : 25.4 * mm});
        }
        {
            var Q0;
            Q0=makeQuery(id+"F11.boolean.opBoolean","MERGE",FACE,{"derivedFrom":[makeQuery(id+"F8.opExtrude","CAP_FACE",FACE,{"disambiguationData":[OSD([sQuery(id+"F4.wireOp",EDGE,"E35"),sQuery(id+"F4.wireOp",EDGE,"E36"),sQuery(id+"F4.wireOp",EDGE,"E37"),sQuery(id+"F4.wireOp",EDGE,"E38"),sQuery(id+"F4.wireOp",EDGE,"E50"),sQuery(id+"F4.wireOp",EDGE,"E51"),sQuery(id+"F4.wireOp",EDGE,"E53"),sQuery(id+"F4.wireOp",EDGE,"E54"),sQuery(id+"F4.wireOp",EDGE,"E56"),sQuery(id+"F4.wireOp",EDGE,"E59"),sQuery(id+"F4.wireOp",EDGE,"E60"),sQuery(id+"F4.wireOp",EDGE,"E61"),sQuery(id+"F4.wireOp",EDGE,"E62"),sQuery(id+"F4.wireOp",EDGE,"E120")])],"isStart":false}),makeQuery(id+"F11.opExtrude","CAP_FACE",FACE,{"disambiguationData":[OSD([sQuery(id+"F4.wireOp",EDGE,"E42"),sQuery(id+"F4.wireOp",EDGE,"E43"),sQuery(id+"F4.wireOp",EDGE,"E45"),sQuery(id+"F4.wireOp",EDGE,"E100")])],"isStart":false}),makeQuery(id+"F11.opExtrude","CAP_FACE",FACE,{"disambiguationData":[OSD([sQuery(id+"F10.wireOp",EDGE,"E167.0"),sQuery(id+"F10.wireOp",EDGE,"E169.0"),sQuery(id+"F10.wireOp",EDGE,"E181.0"),sQuery(id+"F10.wireOp",EDGE,"E182"),sQuery(id+"F10.wireOp",EDGE,"E183")])],"isStart":false})]});
            var sketch = newSketch(context, id + "F14", { "sketchPlane" : qUnion([Q0])});
            skPoint(sketch, "E194.0", {"position": v(-76.45, 75.35) * mm});
            skPoint(sketch, "E195.0", {"position": v(75.68, 76.2) * mm});
            skPoint(sketch, "E196.0", {"position": v(75.68, -76.07) * mm});
            skLineSegment(sketch, "E197", {"start": v(75.68, 76.2) * mm, "end": v(75.68, -76.07) * mm});
            skLineSegment(sketch, "E198", {"start": v(75.68, -76.07) * mm, "end": v(-76.45, -73.26) * mm});
            skLineSegment(sketch, "E199", {"start": v(-76.45, -73.26) * mm, "end": v(-76.45, 75.35) * mm});
            skLineSegment(sketch, "E200", {"start": v(-76.45, 75.35) * mm, "end": v(75.68, 76.2) * mm});
            skSolve(sketch);
        }
        {
            var Q0;
            {var subQ4=sQuery(id+"F14.wireOp",EDGE,"E199");Q0=makeQuery(id+"F14.imprint","IMPRINT",FACE,{"disambiguationData":[TD([[makeQuery(id+"F14.imprint","IMPRINT",EDGE,{"derivedFrom":subQ4}),-1.0]])]});}
            var sketch = newSketch(context, id + "F15", { "sketchPlane" : qUnion([Q0])});
            skLineSegment(sketch, "E201.0", {"start": v(11.47, 17.6) * mm, "end": v(12, -28.89) * mm});
            skPoint(sketch, "E202.0", {"position": v(12, -28.89) * mm});
            skLineSegment(sketch, "E203.0", {"start": v(12.92, -28.89) * mm, "end": v(12.4, 17.61) * mm});
            skLineSegment(sketch, "E204.0", {"start": v(12, -28.89) * mm, "end": v(12.92, -28.89) * mm});
            skLineSegment(sketch, "E205.0", {"start": v(12.4, 17.61) * mm, "end": v(11.47, 17.6) * mm});
            skPoint(sketch, "E206.0", {"position": v(10.67, -28.89) * mm});
            skLineSegment(sketch, "E207.0", {"start": v(8.43, -28.89) * mm, "end": v(12.92, -28.89) * mm});
            skLineSegment(sketch, "E208.0", {"start": v(8.43, -28.89) * mm, "end": v(6.38, -28.89) * mm});
            skLineSegment(sketch, "E209", {"start": v(6.38, -28.89) * mm, "end": v(6.38, -28.14) * mm});
            skLineSegment(sketch, "E210", {"start": v(6.38, -28.14) * mm, "end": v(12, -28.08) * mm});
            skSolve(sketch);
        }
        {
            var Q0;
            Q0 = qSketchRegion(id + "F15", true);
            extrude(context, id + "F16", {"entities" : qUnion([Q0]), "oppositeDirection" : true, "depth" : 25.4 * mm, "offsetDistance" : 25.4 * mm});
        }
    });
